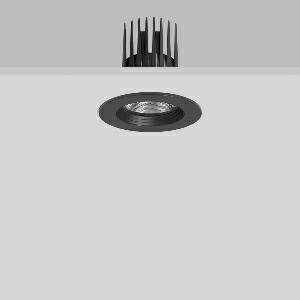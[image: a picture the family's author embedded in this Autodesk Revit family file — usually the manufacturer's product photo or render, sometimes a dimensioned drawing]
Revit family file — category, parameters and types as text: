
# Revit family: heledon_mini_e_901741_003_2_76_d383
name_source: partatom
category: Lighting Fixtures
units: mm (PartAtom-declared; Revit-internal decimal feet)

## family parameters
Cut with Voids When Loaded = No
Host = Face
Light Source = No
Part Type = Normal
Room Calculation Point = No
Round Connector Dimension = Use Diameter
Shared = No

## types (1)
- HELEDON mini E (1 x LED Modul 927, 2300 lm, 2700)
    Apparent Load = 20 VA
    Approval mark = CE
    CIE Flux Codes = 99 100 100 100 100
    Color Rendering = 92
    Color Temperature = 2700
    Default Elevation = 1800 mm
    Description = Series: HELEDON mini
Round recessed downlight. Housing: die-cast aluminium, powder-coated. Black plastic ring and recessed LED to prevent glare from the side. Optical assembly with reflector made of MIRO-Silver with 98% total light reflection for outstanding efficiency - can be changed without tools. Best colour rendering index Ra>90. Suitable for Recessed ceiling mounting. Installation without tools thanks to spring fastening system. Including separate LED converter with connecting cable 600 mm.High quality converter without flickering and stroboscopic effect. Through-wiring box (5 pole) available as accessory. The following accessories can be mounted without use of tools: interchangeable lenses, decorative glasses, honeycomb louvre, clear and frosted diffusers, white interchangeable plastic ring. 
Colour: deep black, matt (RAL 9005)
Diameter: 124 mm
Height: 3 mm
Cut-out diameter: 114 mm
Recess height: 170 mm
Luminaire: recess height: 120 mm
Lamp: LED
Socket: without socket
Colour temperature: 2700K
Colour rendering index (CRI): 92
System power: 20 W
Rated luminous flux: 2300 lm
Luminous efficiency: 115 lm/W
Control gear: Converter, dimmable, DALI
Protection class: II
Type of protection: IP 20
    Height = 0 mm  [stored 0 ft]
    Lamp = 1 x LED Modul 927
    Lamp Light Flux = 2300 lm
    Lamp count = 1
    Length = 124 mm  [stored 0.406824 ft]
    Lifetime = 50000 h
    Luminous efficacy = 115 lm/W
    Manufacturer = RZB
    ModVariant = No
    Model = 901741.003.2.76
    Mounting Place = Ceiling
    Mounting Type = Recessed
    Number of Poles = 1
    OnlyDefault = Yes
    Power Factor = 1
    Product Name = HELEDON mini E
    Product group = Recessed downlights
    ProductGroupID = 402
    Protection Class = Protection class II
    Protection Degree = IP 20
    RLX_Detail_Level = 1
    RLX_Emergency_Light_Flux = 0 lm
    RLX_Emergency_Type = 0
    RLX_Emergency_Type_DB = No
    RlxData = <blob elided: 128297 chars, md5=11c31d2e>
    Socket = socket
    Standby Power = 0 W
    System Light Flux = 2300 lm
    System Power = 20 W
    Type Comments = Product without accessories
    Type Image = 901657.003.jpg
    URL = http://relux.com
    VarID = ---
    Voltage = 230 V
    Voltage Range = 220-240 V
    Weight = 0.00 kg
    Width = 0 mm  [stored 0 ft]

note: [stored X ft] marks values corroborated as IEEE doubles in the binary element streams (Revit-internal decimal feet)

## geometry (parser evidence)
native form markers: Blend x4, Sweep x10
no freeform markers — native parametric forms only
